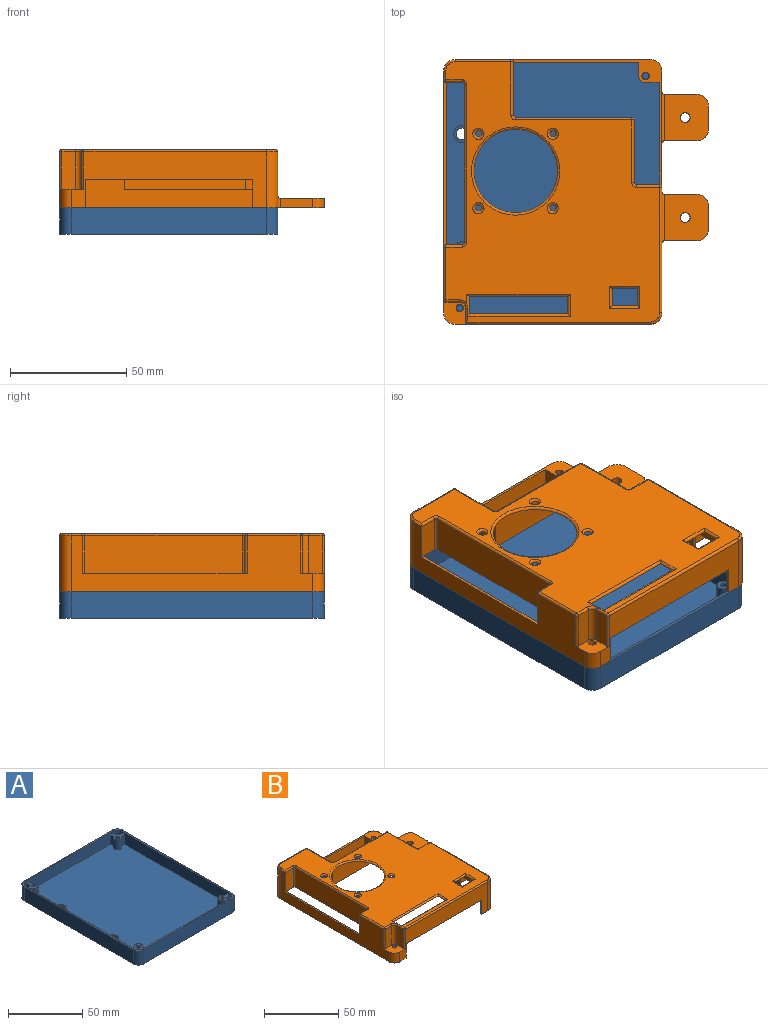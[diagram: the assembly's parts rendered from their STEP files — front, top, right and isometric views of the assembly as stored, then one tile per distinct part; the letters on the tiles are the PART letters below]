
ASSEMBLY  parts=2 mates=1
PART A: 65 faces, bbox 94x114x11.5 mm
  f0: plane 111.6x91.6mm, normal (0,0,1), area 9894.1mm2, adj f8,f9,f10,f14,f15,f20,f25,f26
  f1: plane 4.48x4.48mm, normal (0,0,1), area 13.7mm2, adj f16,f17,f18,f54
  f2: plane 4.48x4.48mm, normal (0,0,1), area 13.7mm2, adj f23,f24,f29,f53
  f3: plane 4.48x4.48mm, normal (0,0,1), area 13.7mm2, adj f5,f6,f7,f51
  f4: plane 4.48x4.48mm, normal (0,0,1), area 13.7mm2, adj f34,f35,f36,f52
  f5: plane 8x3.07mm, normal (-1,0,0), area 24.6mm2, adj f3,f6,f12,f51
  f6: cylinder r=3mm len=8mm, axis (0,0,-1), area 16.2mm2, adj f3,f5,f7,f12
  f7: plane 8x3.07mm, normal (0,1,0), area 24.6mm2, adj f3,f6,f12,f51
  f8: plane 8x3.05mm, normal (0,-1,0), area 24.4mm2, adj f0,f9,f12,f41
  f9: cylinder r=3mm len=8mm, axis (0,0,-1), area 93.3mm2, adj f0,f8,f10,f12
  f10: plane 8x3.05mm, normal (1,0,0), area 24.4mm2, adj f0,f9,f12,f44
  f11: cylinder r=1.4mm len=8mm, axis (0,0,-1), area 70.4mm2, adj f12,f13
  f12: plane 8.8x8.8mm, normal (0,0,1), area 36.6mm2, adj f5,f6,f7,f8,f9,f10,f11,f41
  f13: plane 2.8x2.8mm, normal (0,0,1), area 6.2mm2, adj f11
  f14: cylinder r=3mm len=8mm, axis (0,0,-1), area 93.3mm2, adj f0,f15,f20,f21
  f15: plane 8x3.05mm, normal (0,1,0), area 24.4mm2, adj f0,f14,f21,f41
  f16: plane 8x3.07mm, normal (0,-1,0), area 24.6mm2, adj f1,f17,f21,f54
  f17: cylinder r=3mm len=8mm, axis (0,0,-1), area 16.2mm2, adj f1,f16,f18,f21
  f18: plane 8x3.07mm, normal (-1,0,0), area 24.6mm2, adj f1,f17,f21,f54
  f19: cylinder r=1.4mm len=8mm, axis (0,0,-1), area 70.4mm2, adj f21,f22
  f20: plane 8x3.05mm, normal (1,0,0), area 24.4mm2, adj f0,f14,f21,f42
  f21: plane 8.8x8.8mm, normal (0,0,1), area 36.6mm2, adj f14,f15,f16,f17,f18,f19,f20,f41
  f22: plane 2.8x2.8mm, normal (0,0,1), area 6.2mm2, adj f19
  f23: cylinder r=3mm len=8mm, axis (0,0,-1), area 16.2mm2, adj f2,f24,f29,f30
  f24: plane 8x3.07mm, normal (0,-1,0), area 24.6mm2, adj f2,f23,f30,f53
  f25: plane 8x3.05mm, normal (0,1,0), area 24.4mm2, adj f0,f26,f30,f43
  f26: cylinder r=3mm len=8mm, axis (0,0,-1), area 93.3mm2, adj f0,f25,f27,f30
  f27: plane 8x3.05mm, normal (-1,0,0), area 24.4mm2, adj f0,f26,f30,f42
  f28: cylinder r=1.4mm len=8mm, axis (0,0,-1), area 70.4mm2, adj f30,f31
  f29: plane 8x3.07mm, normal (1,0,0), area 24.6mm2, adj f2,f23,f30,f53
  f30: plane 8.8x8.8mm, normal (0,0,1), area 36.6mm2, adj f23,f24,f25,f26,f27,f28,f29,f42
  f31: plane 2.8x2.8mm, normal (0,0,1), area 6.2mm2, adj f28
  f32: cylinder r=3mm len=8mm, axis (0,0,-1), area 93.3mm2, adj f0,f33,f38,f39
  f33: plane 8x3.05mm, normal (0,-1,0), area 24.4mm2, adj f0,f32,f39,f43
  f34: plane 8x3.07mm, normal (0,1,0), area 24.6mm2, adj f4,f35,f39,f52
  f35: cylinder r=3mm len=8mm, axis (0,0,-1), area 16.2mm2, adj f4,f34,f36,f39
  f36: plane 8x3.07mm, normal (1,0,0), area 24.6mm2, adj f4,f35,f39,f52
  f37: cylinder r=1.4mm len=8mm, axis (0,0,-1), area 70.4mm2, adj f39,f40
  f38: plane 8x3.05mm, normal (-1,0,0), area 24.4mm2, adj f0,f32,f39,f44
  f39: plane 8.8x8.8mm, normal (0,0,1), area 36.6mm2, adj f32,f33,f34,f35,f36,f37,f38,f43
  f40: plane 2.8x2.8mm, normal (0,0,1), area 6.2mm2, adj f37
  f41: plane 101.6x9.5mm, normal (1,0,0), area 933.2mm2, adj f0,f8,f12,f15,f21,f45,f51,f54
  f42: plane 81.6x9.5mm, normal (0,1,0), area 743.2mm2, adj f0,f20,f21,f27,f30,f45,f53,f54
  f43: plane 101.6x9.5mm, normal (-1,0,0), area 933.2mm2, adj f0,f25,f30,f33,f39,f45,f52,f53
  f44: plane 81.6x9.5mm, normal (0,-1,0), area 743.2mm2, adj f0,f10,f12,f38,f39,f45,f51,f52
  f45: plane 114x94mm, normal (0,0,1), area 493.4mm2, adj f41,f42,f43,f44,f47,f48,f49,f50
  f46: plane 114x94mm, normal (0,0,-1), area 10652.1mm2, adj f47,f48,f49,f50,f55,f56,f57,f58
  f47: plane 84x11.5mm, normal (0,1,0), area 966mm2, adj f45,f46,f57,f58
  f48: plane 104x11.5mm, normal (1,0,0), area 1196mm2, adj f45,f46,f56,f57
  f49: plane 84x11.5mm, normal (0,-1,0), area 966mm2, adj f45,f46,f55,f56
  f50: plane 104x11.5mm, normal (-1,0,0), area 1196mm2, adj f45,f46,f55,f58
  f51: cylinder r=5mm len=9.5mm, axis (0,0,-1), area 66.6mm2, adj f3,f5,f7,f12,f41,f44,f45
  f52: cylinder r=5mm len=9.5mm, axis (0,0,-1), area 66.6mm2, adj f4,f34,f36,f39,f43,f44,f45
  f53: cylinder r=5mm len=9.5mm, axis (0,0,1), area 66.6mm2, adj f2,f24,f29,f30,f42,f43,f45
  f54: cylinder r=5mm len=9.5mm, axis (0,0,1), area 66.6mm2, adj f1,f16,f18,f21,f41,f42,f45
  f55: cylinder r=5mm len=11.5mm, axis (0,0,1), area 90.3mm2, adj f45,f46,f49,f50
  f56: cylinder r=5mm len=11.5mm, axis (0,0,-1), area 90.3mm2, adj f45,f46,f48,f49
  f57: cylinder r=5mm len=11.5mm, axis (0,0,1), area 90.3mm2, adj f45,f46,f47,f48
  f58: cylinder r=5mm len=11.5mm, axis (0,0,-1), area 90.3mm2, adj f45,f46,f47,f50
  f59: cylinder r=2.6mm len=5.2mm, axis (0,0,-1), area 65.3mm2, adj f46,f64
  f60: cylinder r=2.6mm len=5.2mm, axis (0,0,-1), area 65.3mm2, adj f46,f62
  f61: cylinder r=3.6mm len=7.2mm, axis (0,0,-1), area 45.2mm2, adj f0,f62
  f62: plane 7.2x7.2mm, normal (0,0,1), area 19.5mm2, adj f60,f61
  f63: cylinder r=3.6mm len=7.2mm, axis (0,0,-1), area 45.2mm2, adj f0,f64
  f64: plane 7.2x7.2mm, normal (0,0,1), area 19.5mm2, adj f59,f63
PART B: 124 faces, bbox 114.4x114.8x25 mm
  f0: plane 104x24mm, normal (1,0,0), area 1320mm2, adj f4,f17,f21,f28,f30,f42,f43,f44
  f1: plane 97.8x24mm, normal (1,0,0), area 1163.2mm2, adj f3,f4,f24,f26,f41,f50,f52,f53
  f2: plane 77.8x24mm, normal (0,-1,0), area 971.2mm2, adj f3,f4,f10,f21,f26,f46,f49
  f3: plane 111.6x91.6mm, normal (0,0,-1), area 5924.3mm2, adj f1,f2,f5,f11,f22,f23,f24,f25
  f4: plane 114x114mm, normal (0,0,-1), area 1234mm2, adj f0,f1,f2,f5,f6,f8,f9,f10
  f5: plane 97.8x24mm, normal (-1,0,0), area 1455.2mm2, adj f3,f4,f8,f17,f21,f25,f42,f43
  f6: plane 84x24mm, normal (0,1,0), area 1056mm2, adj f4,f21,f28,f29,f77,f83
  f7: plane 112x92mm, normal (0,0,1), area 5866.6mm2, adj f72,f74,f75,f78,f79,f81,f83,f85
  f8: plane 8x5.8mm, normal (0,-1,0), area 46.4mm2, adj f4,f5,f9,f21
  f9: cylinder r=3mm len=8mm, axis (0,0,-1), area 37.7mm2, adj f4,f8,f10,f21
  f10: plane 8x5.8mm, normal (-1,0,0), area 46.4mm2, adj f2,f4,f9,f21
  f11: plane 77.8x24mm, normal (0,1,0), area 1003.2mm2, adj f3,f4,f17,f23,f25,f31,f32,f33
  f12: plane 16x6mm, normal (0,-1,0), area 96mm2, adj f13,f19,f106,f107
  f13: cylinder r=2.5mm len=16mm, axis (0,0,-1), area 62.8mm2, adj f12,f14,f19,f103
  f14: plane 16x6mm, normal (-1,0,0), area 96mm2, adj f13,f19,f93,f101
  f15: plane 84x24mm, normal (0,-1,0), area 1064mm2, adj f4,f17,f19,f27,f30,f31,f32,f33
  f16: plane 104x24mm, normal (-1,0,0), area 1272mm2, adj f4,f19,f27,f29,f40,f41,f87,f104
  f17: plane 18x11mm, normal (0,0,-1), area 33.4mm2, adj f0,f5,f11,f15,f25,f30,f31,f44
  f18: cylinder r=1.6mm len=8mm, axis (0,0,-1), area 80.4mm2, adj f4,f19
  f19: plane 10.5x10.5mm, normal (0,0,1), area 75.9mm2, adj f12,f13,f14,f15,f16,f18,f27,f93
  f20: cylinder r=1.6mm len=8mm, axis (0,0,-1), area 80.4mm2, adj f4,f21
  f21: plane 65x55mm, normal (0,0,1), area 202.7mm2, adj f0,f2,f5,f6,f8,f9,f10,f20
  f22: cylinder r=3mm len=24mm, axis (0,0,-1), area 113.1mm2, adj f3,f4,f23,f24
  f23: plane 24x5.8mm, normal (1,0,0), area 139.2mm2, adj f3,f4,f11,f22
  f24: plane 24x5.8mm, normal (0,1,0), area 139.2mm2, adj f1,f3,f4,f22
  f25: cylinder r=5mm len=24mm, axis (0,0,1), area 188.5mm2, adj f3,f5,f11,f17
  f26: cylinder r=5mm len=24mm, axis (0,0,-1), area 188.5mm2, adj f1,f2,f3,f4
  f27: cylinder r=5mm len=8mm, axis (0,0,-1), area 62.8mm2, adj f4,f15,f16,f19
  f28: cylinder r=5mm len=8mm, axis (0,0,-1), area 62.8mm2, adj f0,f4,f6,f21
  f29: cylinder r=5mm len=24mm, axis (0,0,1), area 188.5mm2, adj f4,f6,f16,f85
  f30: cylinder r=5mm len=24mm, axis (0,0,1), area 188.5mm2, adj f0,f15,f17,f88
  f31: plane 12x1.2mm, normal (-1,0,0), area 14.4mm2, adj f11,f15,f17,f32
  f32: plane 72x1.2mm, normal (0,0,-1), area 86.4mm2, adj f11,f15,f31,f33
  f33: plane 12x1.2mm, normal (1,0,0), area 14.4mm2, adj f4,f11,f15,f32
  f34: plane 27x16mm, normal (1,0,0), area 432mm2, adj f49,f70,f75,f76
  f35: plane 23x16mm, normal (1,0,0), area 368mm2, adj f21,f49,f71,f77,f78
  f36: plane 50x16mm, normal (0,1,0), area 800mm2, adj f49,f70,f71,f72
  f37: plane 16x10mm, normal (0,1,0), area 160mm2, adj f21,f49,f76,f81,f82
  f38: plane 68x16mm, normal (-1,0,0), area 1088mm2, adj f53,f89,f98,f99
  f39: plane 16x7mm, normal (0,1,0), area 112mm2, adj f41,f53,f98,f104,f105
  f40: plane 16x8mm, normal (0,-1,0), area 128mm2, adj f16,f41,f53,f89,f90
  f41: plane 71x1.2mm, normal (0,0,1), area 84.2mm2, adj f1,f16,f39,f40,f104
  f42: plane 12x1.2mm, normal (0,-1,0), area 14.4mm2, adj f0,f4,f5,f43
  f43: plane 13x1.2mm, normal (0,0,-1), area 15.6mm2, adj f0,f5,f42,f44
  f44: plane 12x1.2mm, normal (0,1,0), area 14.4mm2, adj f0,f5,f17,f43
  f45: plane 52x16mm, normal (0,-1,0), area 832mm2, adj f3,f46,f48,f49
  f46: plane 25.8x16mm, normal (-1,0,0), area 412.8mm2, adj f2,f3,f45,f49
  f47: plane 16x12.8mm, normal (0,-1,0), area 204.8mm2, adj f3,f5,f48,f49
  f48: plane 29x16mm, normal (-1,0,0), area 464mm2, adj f3,f45,f47,f49
  f49: plane 64.8x54.8mm, normal (0,0,-1), area 235.4mm2, adj f2,f5,f34,f35,f36,f37,f45,f46
  f50: plane 16x9.8mm, normal (0,1,0), area 156.8mm2, adj f1,f3,f51,f53
  f51: plane 74x16mm, normal (1,0,0), area 1184mm2, adj f3,f50,f52,f53
  f52: plane 16x9.8mm, normal (0,-1,0), area 156.8mm2, adj f1,f3,f51,f53
  f53: plane 74x9.8mm, normal (0,0,-1), area 179.6mm2, adj f1,f38,f39,f40,f50,f51,f52,f89
  f54: plane 14x4mm, normal (0,1,0), area 56mm2, adj f4,f55,f68,f123
  f55: plane 20x19mm, normal (0,0,1), area 355.4mm2, adj f54,f56,f57,f63,f69,f122,f123
  f56: plane 14x4mm, normal (0,-1,0), area 56mm2, adj f4,f55,f67,f122
  f57: plane 10x4mm, normal (1,0,0), area 40mm2, adj f4,f55,f122,f123
  f58: plane 14x4mm, normal (0,1,0), area 56mm2, adj f4,f59,f64,f121
  f59: plane 20x19mm, normal (0,0,1), area 355.4mm2, adj f58,f60,f61,f62,f65,f120,f121
  f60: plane 14x4mm, normal (0,-1,0), area 56mm2, adj f4,f59,f66,f120
  f61: plane 10x4mm, normal (1,0,0), area 40mm2, adj f4,f59,f120,f121
  f62: cylinder r=2.1mm len=4.2mm, axis (0,0,1), area 52.8mm2, adj f4,f59
  f63: cylinder r=2.1mm len=4.2mm, axis (0,0,1), area 52.8mm2, adj f4,f55
  f64: cylinder r=1mm len=5mm, axis (0,0,1), area 6.9mm2, adj f0,f4,f58,f65
  f65: cylinder r=1mm len=22mm, axis (0,-1,0), area 32.6mm2, adj f0,f59,f64,f66
  f66: cylinder r=1mm len=5mm, axis (0,0,-1), area 6.9mm2, adj f0,f4,f60,f65
  f67: cylinder r=1mm len=5mm, axis (0,0,-1), area 6.9mm2, adj f0,f4,f56,f69
  f68: cylinder r=1mm len=5mm, axis (0,0,1), area 6.9mm2, adj f0,f4,f54,f69
  f69: cylinder r=1mm len=22mm, axis (0,-1,0), area 32.6mm2, adj f0,f55,f67,f68
  f70: cylinder r=1mm len=16mm, axis (0,0,-1), area 25.1mm2, adj f34,f36,f49,f73
  f71: cylinder r=1mm len=16mm, axis (0,0,-1), area 25.1mm2, adj f35,f36,f49,f74
  f72: cylinder r=1mm len=50mm, axis (-1,0,0), area 78.5mm2, adj f7,f36,f73,f74
  f73: sphere r=1mm, area 1.6mm2, adj f70,f72,f75
  f74: torus R=2mm, axis (0,0,1), area 3.4mm2, adj f7,f71,f72,f78
  f75: cylinder r=1mm len=27mm, axis (0,1,0), area 42.4mm2, adj f7,f34,f73,f79
  f76: cylinder r=1mm len=16mm, axis (0,0,-1), area 25.1mm2, adj f34,f37,f49,f79
  f77: cylinder r=1mm len=16mm, axis (0,0,1), area 25.1mm2, adj f6,f21,f35,f80
  f78: cylinder r=1mm len=23mm, axis (0,1,0), area 36.1mm2, adj f7,f35,f74,f80
  f79: torus R=2mm, axis (0,0,1), area 3.4mm2, adj f7,f75,f76,f81
  f80: sphere r=1mm, area 1.6mm2, adj f77,f78,f83
  f81: cylinder r=1mm len=10mm, axis (-1,0,0), area 15.7mm2, adj f7,f37,f79,f84
  f82: cylinder r=1mm len=16mm, axis (0,0,-1), area 25.1mm2, adj f0,f21,f37,f84
  f83: cylinder r=1mm len=24mm, axis (1,0,0), area 37.7mm2, adj f6,f7,f80,f85
  f84: sphere r=1mm, area 1.6mm2, adj f81,f82,f86
  f85: torus R=4mm, axis (0,0,1), area 11.4mm2, adj f7,f29,f83,f87
  f86: cylinder r=1mm len=54mm, axis (0,-1,0), area 84.8mm2, adj f0,f7,f84,f88
  f87: cylinder r=1mm len=4.75mm, axis (0,1,0), area 6.9mm2, adj f7,f16,f85,f90
  f88: torus R=4mm, axis (0,0,1), area 11.4mm2, adj f7,f30,f86,f92
  f89: cylinder r=1mm len=16mm, axis (0,0,-1), area 25.1mm2, adj f38,f40,f53,f94
  f90: cylinder r=1mm len=8mm, axis (1,0,0), area 12mm2, adj f7,f40,f87,f94
  f91: cylinder r=1mm len=9.5mm, axis (0,-1,0), area 12.9mm2, adj f3,f7,f95,f96
  f92: cylinder r=1mm len=78.5mm, axis (-1,0,0), area 123.3mm2, adj f7,f15,f88,f97
  f93: cylinder r=1mm len=16mm, axis (0,0,-1), area 25.1mm2, adj f14,f15,f19,f97
  f94: torus R=2mm, axis (0,0,1), area 3.4mm2, adj f7,f89,f90,f99
  f95: cylinder r=1mm len=44.5mm, axis (1,0,0), area 67.9mm2, adj f3,f7,f91,f100
  f96: cylinder r=1mm len=44.25mm, axis (-1,0,0), area 67.8mm2, adj f3,f7,f91,f100,f101
  f97: sphere r=1mm, area 1.6mm2, adj f92,f93,f101
  f98: cylinder r=1mm len=16mm, axis (0,0,1), area 25.1mm2, adj f38,f39,f53,f102
  f99: cylinder r=1mm len=68mm, axis (0,-1,0), area 106.8mm2, adj f7,f38,f94,f102
  f100: cylinder r=1mm len=9.25mm, axis (0,1,0), area 11.8mm2, adj f3,f7,f95,f96,f101,f103
  f101: cylinder r=1mm len=6mm, axis (0,1,0), area 8.6mm2, adj f7,f14,f96,f97,f100,f103
  f102: torus R=2mm, axis (0,0,1), area 3.4mm2, adj f7,f98,f99,f105
  f103: torus R=3.5mm, axis (0,0,1), area 6.8mm2, adj f7,f13,f100,f101,f106
  f104: cylinder r=1mm len=16mm, axis (0,0,1), area 25.1mm2, adj f16,f39,f41,f108
  f105: cylinder r=1mm len=7mm, axis (-1,0,0), area 11mm2, adj f7,f39,f102,f108
  f106: cylinder r=1mm len=6mm, axis (-1,0,0), area 9.4mm2, adj f7,f12,f103,f109
  f107: cylinder r=1mm len=16mm, axis (0,0,1), area 25.1mm2, adj f12,f16,f19,f109
  f108: sphere r=1mm, area 1.6mm2, adj f104,f105,f110
  f109: sphere r=1mm, area 1.6mm2, adj f106,f107,f110
  f110: cylinder r=1mm len=22.75mm, axis (0,1,0), area 35.7mm2, adj f7,f16,f108,f109
  f111: torus R=2.4mm, axis (0,0,1), area 17.4mm2, adj f3,f7
  f112: torus R=2.4mm, axis (0,0,1), area 17.4mm2, adj f3,f7
  f113: torus R=2.4mm, axis (0,0,1), area 17.4mm2, adj f3,f7
  f114: torus R=2.4mm, axis (0,0,1), area 17.4mm2, adj f3,f7
  f115: torus R=19mm, axis (0,0,1), area 181.2mm2, adj f3,f7
  f116: cylinder r=1mm len=13mm, axis (1,0,0), area 18.4mm2, adj f3,f7,f117,f118
  f117: cylinder r=1mm len=9.5mm, axis (0,1,0), area 12.9mm2, adj f3,f7,f116,f119
  f118: cylinder r=1mm len=9.5mm, axis (0,-1,0), area 12.9mm2, adj f3,f7,f116,f119
  f119: cylinder r=1mm len=13mm, axis (-1,0,0), area 18.4mm2, adj f3,f7,f117,f118
  f120: cylinder r=5mm len=5mm, axis (0,0,1), area 31.4mm2, adj f4,f59,f60,f61
  f121: cylinder r=5mm len=5mm, axis (0,0,-1), area 31.4mm2, adj f4,f58,f59,f61
  f122: cylinder r=5mm len=5mm, axis (0,0,1), area 31.4mm2, adj f4,f55,f56,f57
  f123: cylinder r=5mm len=5mm, axis (0,0,-1), area 31.4mm2, adj f4,f54,f55,f57
PLACE A t=(-3.16,-10.54,19.89)mm
PLACE B t=(-140.23,-10.55,29.39)mm
MATE fastened B.f13 <-> A.f14  axis (0,0,-1) through (-84.46,-58.68,29.39)mm
